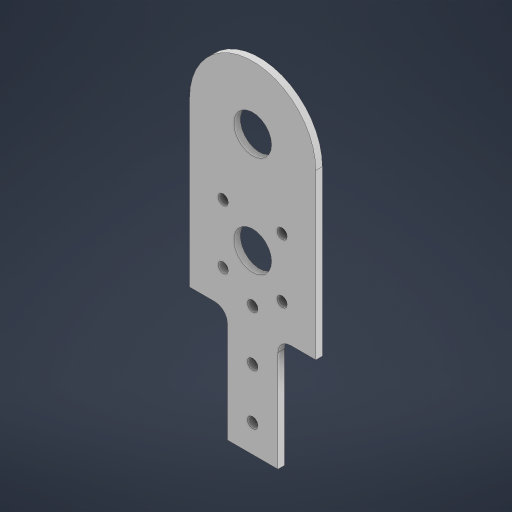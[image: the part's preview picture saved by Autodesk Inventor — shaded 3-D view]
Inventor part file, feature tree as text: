
AUTODESK INVENTOR PART (.ipt)
format: ipt  version: 2024 (Build 280153000, 153)  size: 230,912 bytes
history: native  units: in
note: dims shown in document units (in); Inventor stores cm internally (conversion verified against a paired STEP export)
features: fillet x4, sketch x2, extrude x1, hole x1
ambient origin geometry x8: Origin, YZ Plane, XZ Plane, XY Plane, X Axis, Y Axis, Z Axis, Center Point
bodies: Solid1 (feature_tree)
feature tree (8):
  sketch  "Sketch1"  dims[d0=2.5in d1=5.0in d3=4.2in d4=1.25in]
  extrude  "Extrusion1"  Depth=5.0in
  fillet  "Fillet1"  Radius=4.2in
  fillet  "Fillet2"  Radius=1.25in
  hole  "Hole1"  [1 undecoded]
  fillet  "Fillet5"  Radius=1.25in
  fillet  "Fillet6"  Radius=1.25in
  sketch  "Sketch3"  dims[d5=3.25in d6=0.13in d7=0.0in d8=1.25in d9=1.25in d12=0.748in d13=0.748in d14=0.209in d16=1.65in d17=0.201in d18=0.75in d19=0.385in d20=0.25in d21=0.5635in d22=0.64in d23=0.8108in d28=135.0deg d29=1.0in d30=1.0in d31=1.0in d32=1.0in d33=1.75in d34=0.25in d35=0.25in]
note: 1 required parameter value undecoded (feature->parameter linkage not recoverable at this tier; creation-order binding heuristic only, values carry confidence <= 0.55)
